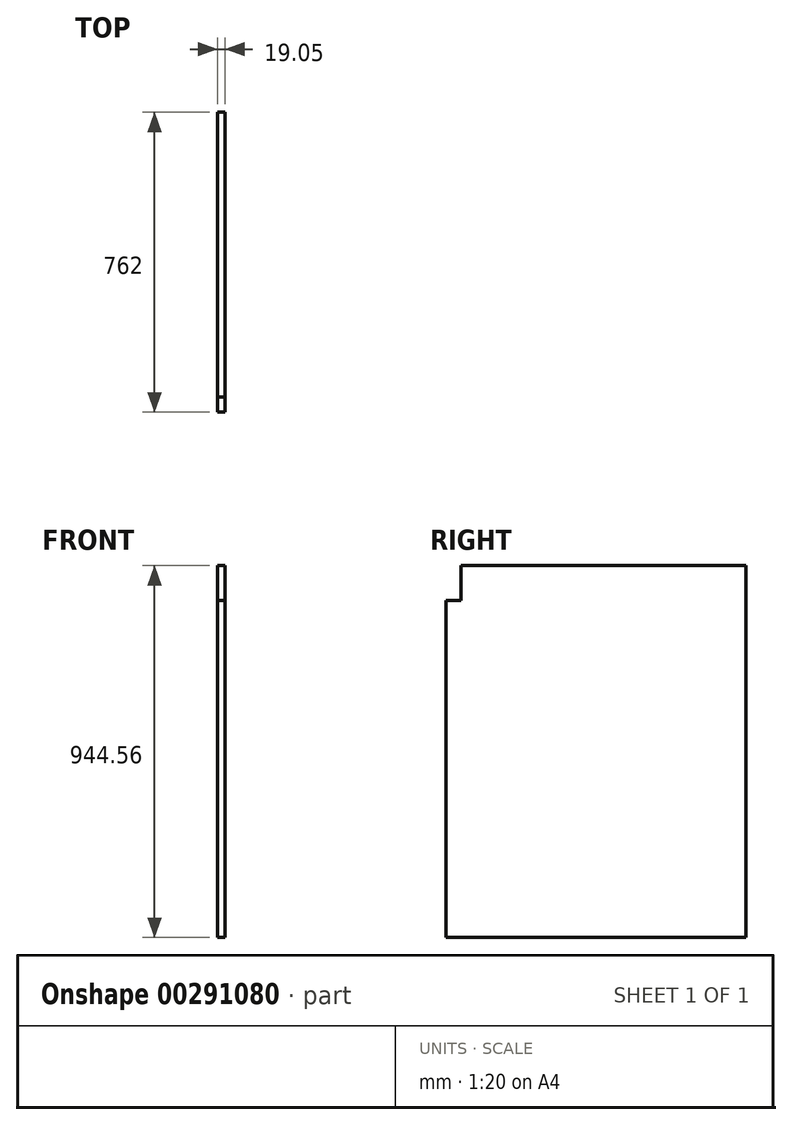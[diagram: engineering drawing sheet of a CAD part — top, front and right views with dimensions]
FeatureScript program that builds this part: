
annotation { "Feature Type Name" : "Feature", "Feature Type Description" : "" }
export const myFeature = defineFeature(function(context is Context, id is Id, definition is map)
    precondition{}
    {
        {
            var Q0;
            Q0=qCreatedBy(makeId("Right.planeOp"),FACE);
            var sketch = newSketch(context, id + "F0", { "sketchPlane" : qUnion([Q0])});
            skLineSegment(sketch, "E0.bottom", {"start": v(0, 0) * mm, "end": v(762, 0) * mm});
            skLineSegment(sketch, "E0.top", {"start": v(0, -944.56) * mm, "end": v(762, -944.56) * mm});
            skLineSegment(sketch, "E0.left", {"start": v(0, 0) * mm, "end": v(0, -944.56) * mm});
            skLineSegment(sketch, "E0.right", {"start": v(762, 0) * mm, "end": v(762, -944.56) * mm});
            skSolve(sketch);
        }
        {
            var Q0;
            Q0 = qSketchRegion(id + "F0", true);
            extrude(context, id + "F1", {"entities" : qUnion([Q0]), "depth" : 19.05 * mm});
        }
        {
            var Q0;
            Q0=qCreatedBy(makeId("Right.planeOp"),FACE);
            var sketch = newSketch(context, id + "F2", { "sketchPlane" : qUnion([Q0])});
            skLineSegment(sketch, "E1.bottom", {"start": v(0, 0) * mm, "end": v(38.1, 0) * mm});
            skLineSegment(sketch, "E1.top", {"start": v(0, -88.9) * mm, "end": v(38.1, -88.9) * mm});
            skLineSegment(sketch, "E1.left", {"start": v(0, 0) * mm, "end": v(0, -88.9) * mm});
            skLineSegment(sketch, "E1.right", {"start": v(38.1, 0) * mm, "end": v(38.1, -88.9) * mm});
            skSolve(sketch);
        }
        {
            var Q0;
            Q0 = qSketchRegion(id + "F2", true);
            extrude(context, id + "F3", {"entities" : qUnion([Q0]), "operationType" : NewBodyOperationType.REMOVE, "endBound" : BoundingType.THROUGH_ALL, "depth" : 25.4 * mm});
        }
    });
